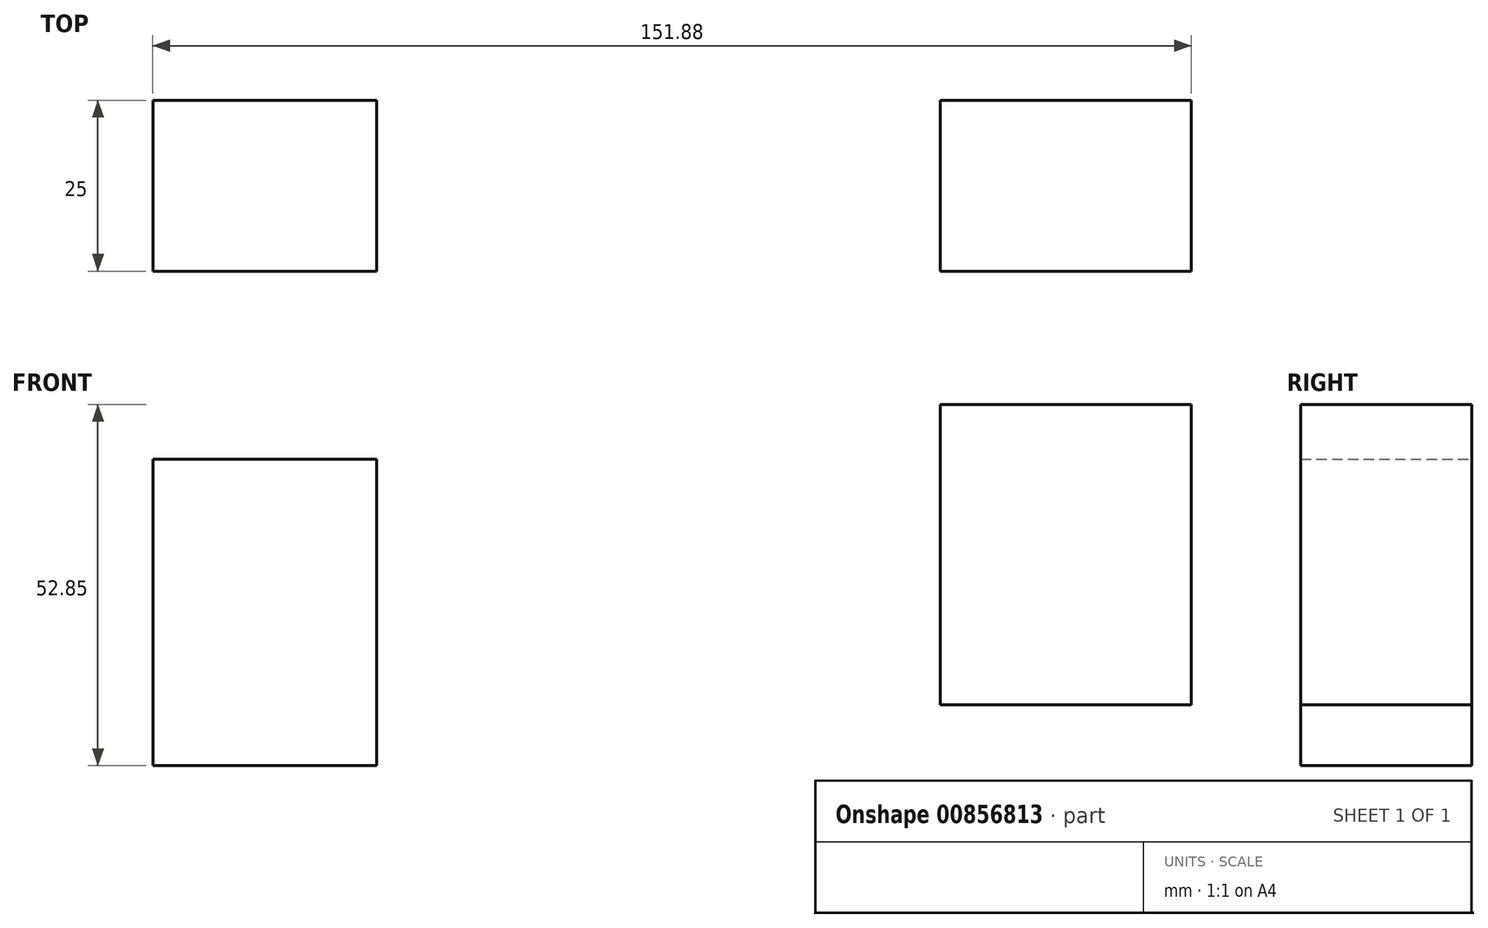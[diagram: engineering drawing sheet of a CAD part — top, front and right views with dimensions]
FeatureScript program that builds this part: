
annotation { "Feature Type Name" : "Feature", "Feature Type Description" : "" }
export const myFeature = defineFeature(function(context is Context, id is Id, definition is map)
    precondition{}
    {
        {
            var Q0;
            Q0=qCreatedBy(makeId("Front.planeOp"),FACE);
            var sketch = newSketch(context, id + "F0", { "sketchPlane" : qUnion([Q0])});
            skLineSegment(sketch, "E0.bottom", {"start": v(-123.84, 24.17) * mm, "end": v(-91.12, 24.17) * mm});
            skLineSegment(sketch, "E0.top", {"start": v(-123.84, 69) * mm, "end": v(-91.12, 69) * mm});
            skLineSegment(sketch, "E0.left", {"start": v(-123.84, 24.17) * mm, "end": v(-123.84, 69) * mm});
            skLineSegment(sketch, "E0.right", {"start": v(-91.12, 24.17) * mm, "end": v(-91.12, 69) * mm});
            skPoint(sketch, "E0.middle", {"position": v(-107.48, 46.58) * mm});
            skLineSegment(sketch, "E1.bottom", {"start": v(-8.68, 33.04) * mm, "end": v(28.04, 33.04) * mm});
            skLineSegment(sketch, "E1.top", {"start": v(-8.68, 77.02) * mm, "end": v(28.04, 77.02) * mm});
            skLineSegment(sketch, "E1.left", {"start": v(-8.68, 33.04) * mm, "end": v(-8.68, 77.02) * mm});
            skLineSegment(sketch, "E1.right", {"start": v(28.04, 33.04) * mm, "end": v(28.04, 77.02) * mm});
            skPoint(sketch, "E1.middle", {"position": v(9.68, 55.03) * mm});
            skSolve(sketch);
        }
        {
            var Q0;
            Q0=makeQuery(id+"F0.imprint","IMPRINT",FACE,{"disambiguationData":[TD([[makeQuery(id+"F0.imprint","IMPRINT",EDGE,{"derivedFrom":sQuery(id+"F0.wireOp",EDGE,"E0.bottom")}),1.0]])]});
            var Q1;
            Q1=makeQuery(id+"F0.imprint","IMPRINT",FACE,{"disambiguationData":[TD([[makeQuery(id+"F0.imprint","IMPRINT",EDGE,{"derivedFrom":sQuery(id+"F0.wireOp",EDGE,"E1.bottom")}),1.0]])]});
            extrude(context, id + "F1", {"entities" : qUnion([Q0, Q1]), "depth" : 25 * mm, "offsetDistance" : 25 * mm});
        }
    });
